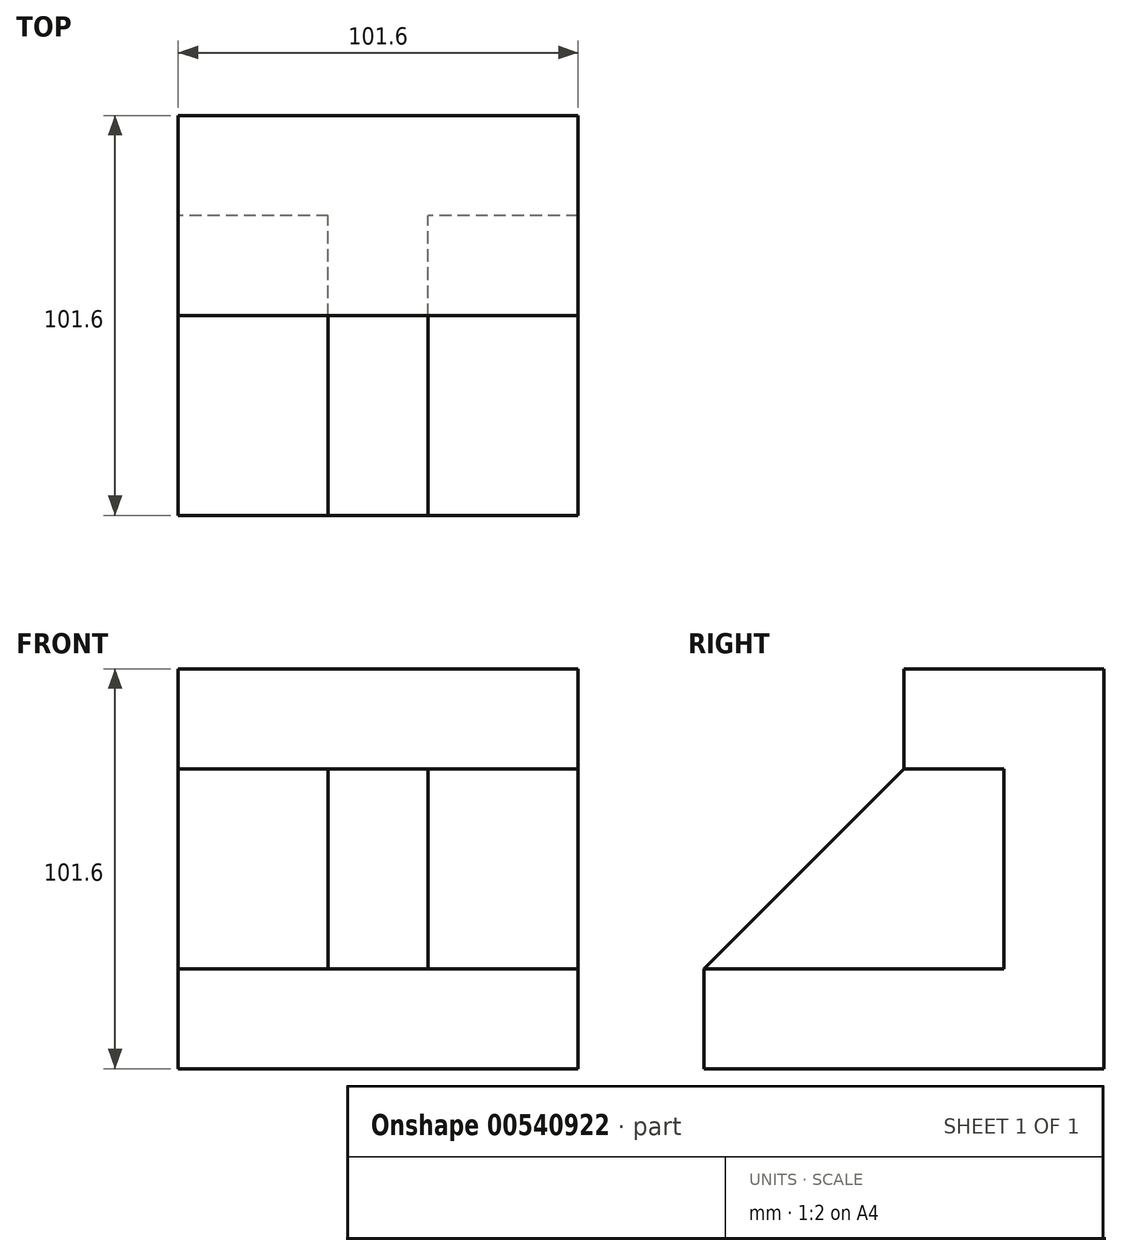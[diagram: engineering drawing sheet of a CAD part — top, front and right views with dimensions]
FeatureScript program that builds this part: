
annotation { "Feature Type Name" : "Feature", "Feature Type Description" : "" }
export const myFeature = defineFeature(function(context is Context, id is Id, definition is map)
    precondition{}
    {
        {
            var Q0;
            Q0=qCreatedBy(makeId("Right.planeOp"),FACE);
            var sketch = newSketch(context, id + "F0", { "sketchPlane" : qUnion([Q0])});
            skLineSegment(sketch, "E0", {"start": v(0, 0) * mm, "end": v(0, 76.2) * mm});
            skLineSegment(sketch, "E1", {"start": v(0, 76.2) * mm, "end": v(-50.8, 76.2) * mm});
            skLineSegment(sketch, "E2", {"start": v(-50.8, 76.2) * mm, "end": v(-50.8, 50.8) * mm});
            skLineSegment(sketch, "E3", {"start": v(-50.8, 50.8) * mm, "end": v(-25.4, 50.8) * mm});
            skLineSegment(sketch, "E4", {"start": v(-25.4, 50.8) * mm, "end": v(-25.4, 0) * mm});
            skLineSegment(sketch, "E5", {"start": v(0, 0) * mm, "end": v(0, -25.4) * mm});
            skLineSegment(sketch, "E6", {"start": v(0, -25.4) * mm, "end": v(-101.6, -25.4) * mm});
            skLineSegment(sketch, "E7", {"start": v(-25.4, 0) * mm, "end": v(-101.6, 0) * mm});
            skLineSegment(sketch, "E8", {"start": v(-101.6, 0) * mm, "end": v(-101.6, -25.4) * mm});
            skSolve(sketch);
        }
        {
            var Q0;
            Q0=makeQuery(id+"F0.imprint","IMPRINT",FACE,{"disambiguationData":[TD([[makeQuery(id+"F0.imprint","IMPRINT",EDGE,{"derivedFrom":sQuery(id+"F0.wireOp",EDGE,"E0")}),1.0]])]});
            extrude(context, id + "F1", {"entities" : qUnion([Q0]), "depth" : 101.6 * mm, "offsetDistance" : 25.4 * mm});
        }
        {
            var Q0;
            Q0=makeQuery(id+"F1.opExtrude","SWEPT_FACE",FACE,{"disambiguationData":[OSD([sQuery(id+"F0.wireOp",EDGE,"E4")])]});
            var sketch = newSketch(context, id + "F2", { "sketchPlane" : qUnion([Q0])});
            skLineSegment(sketch, "E9", {"start": v(0, 0) * mm, "end": v(38.1, 0) * mm});
            skLineSegment(sketch, "E10", {"start": v(101.6, 0) * mm, "end": v(63.5, 0) * mm});
            skLineSegment(sketch, "E11", {"start": v(63.5, 0) * mm, "end": v(63.5, 50.8) * mm});
            skLineSegment(sketch, "E12", {"start": v(38.1, 0) * mm, "end": v(38.1, 50.8) * mm});
            skSolve(sketch);
        }
        {
            var Q0;
            {var subQ0=sQuery(id+"F2.wireOp",EDGE,"E11");Q0=makeQuery(id+"F2.imprint","IMPRINT",FACE,{"disambiguationData":[TD([[makeQuery(id+"F2.imprint","IMPRINT",EDGE,{"derivedFrom":subQ0}),1.0]])]});}
            extrude(context, id + "F3", {"entities" : qUnion([Q0]), "operationType" : NewBodyOperationType.ADD, "depth" : 76.2 * mm, "offsetDistance" : 25.4 * mm});
        }
        {
            var Q0;
            Q0=makeQuery(id+"F3.opExtrude","SWEPT_FACE",FACE,{"disambiguationData":[OSD([sQuery(id+"F2.wireOp",EDGE,"E12")])]});
            var sketch = newSketch(context, id + "F4", { "sketchPlane" : qUnion([Q0])});
            skLineSegment(sketch, "E13", {"start": v(50.8, 50.8) * mm, "end": v(101.6, 0) * mm});
            skSolve(sketch);
        }
        {
            var Q0;
            Q0=makeQuery(id+"F4.imprint","IMPRINT",FACE,{"disambiguationData":[TD([[makeQuery(id+"F4.imprint","IMPRINT",EDGE,{"derivedFrom":sQuery(id+"F4.wireOp",EDGE,"E13")}),1.0]])]});
            extrude(context, id + "F5", {"entities" : qUnion([Q0]), "operationType" : NewBodyOperationType.REMOVE, "oppositeDirection" : true, "depth" : 25.4 * mm, "offsetDistance" : 25.4 * mm});
        }
    });
